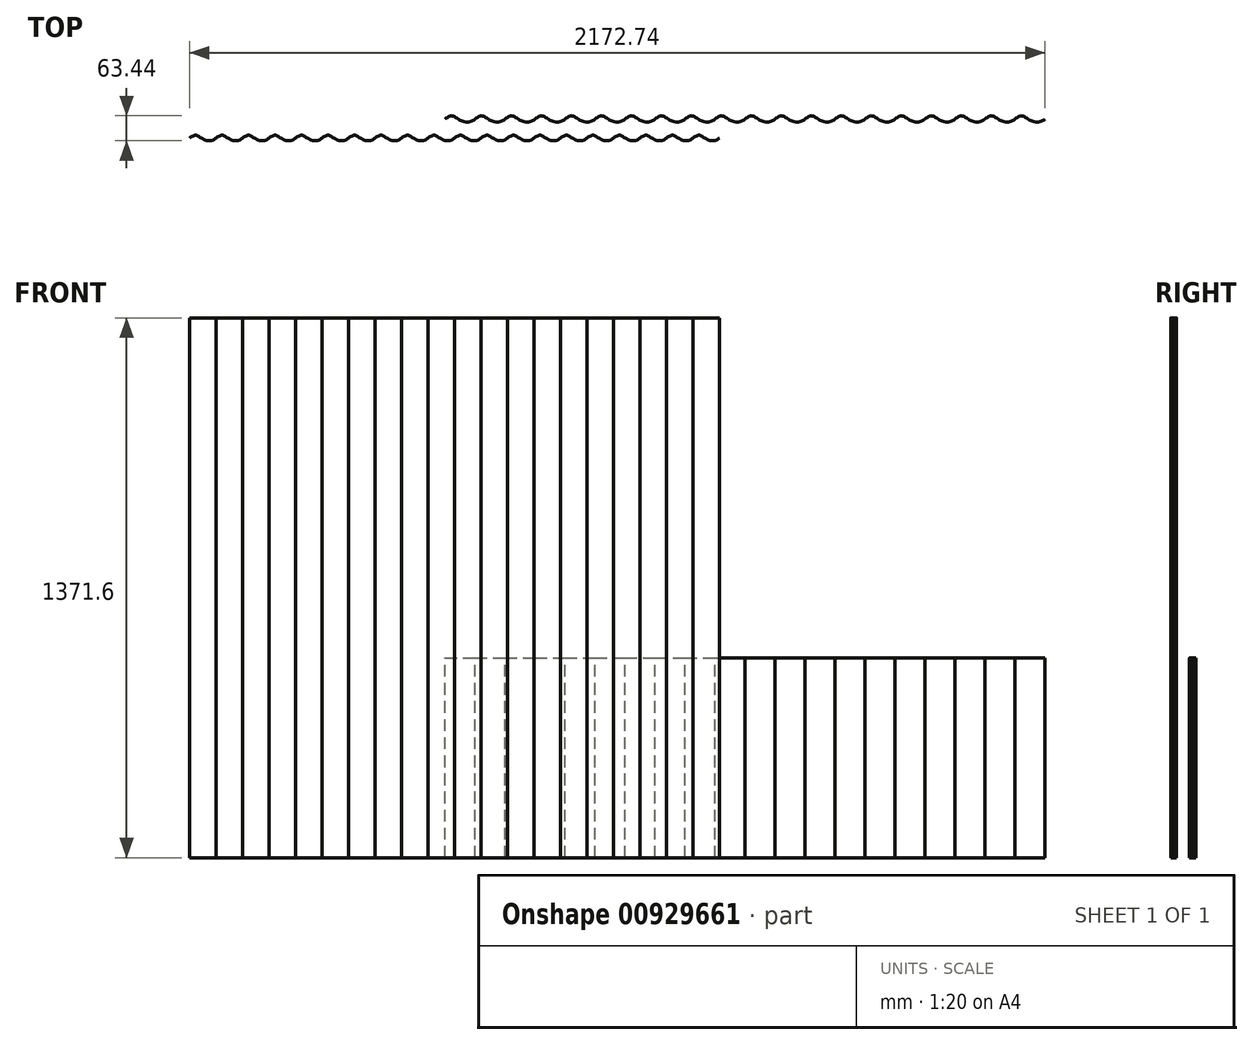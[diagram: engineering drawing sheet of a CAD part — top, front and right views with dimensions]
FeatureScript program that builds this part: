
annotation { "Feature Type Name" : "Feature", "Feature Type Description" : "" }
export const myFeature = defineFeature(function(context is Context, id is Id, definition is map)
    precondition{}
    {
        {
            var Q0;
            Q0=qCreatedBy(makeId("Top.planeOp"),FACE);
            var sketch = newSketch(context, id + "F0", { "sketchPlane" : qUnion([Q0])});
            skFitSpline(sketch, "E0", {"points": [v(-76.2, 0) * mm, v(-59.35, 8.43) * mm, v(-42.5, 0) * mm, v(-18.32, -7.7) * mm, v(0, 0) * mm], "startDerivative": vector(71.9, 53.55) * mm, "endDerivative": vector(70.3, 44.56) * mm});
            skFitSpline(sketch, "E1", {"points": [v(0, 0) * mm, v(16.85, 8.43) * mm, v(33.7, 0) * mm, v(57.88, -7.7) * mm, v(76.2, 0) * mm], "startDerivative": vector(71.9, 53.55) * mm, "endDerivative": vector(70.3, 44.56) * mm});
            skFitSpline(sketch, "E2", {"points": [v(76.2, 0) * mm, v(93.05, 8.43) * mm, v(109.9, 0) * mm, v(134.08, -7.7) * mm, v(152.4, 0) * mm], "startDerivative": vector(71.9, 53.55) * mm, "endDerivative": vector(70.3, 44.56) * mm});
            skFitSpline(sketch, "E3", {"points": [v(152.4, 0) * mm, v(169.25, 8.43) * mm, v(186.1, 0) * mm, v(210.28, -7.7) * mm, v(228.6, 0) * mm], "startDerivative": vector(71.9, 53.55) * mm, "endDerivative": vector(70.3, 44.56) * mm});
            skFitSpline(sketch, "E4", {"points": [v(228.6, 0) * mm, v(245.45, 8.43) * mm, v(262.3, 0) * mm, v(286.48, -7.7) * mm, v(304.8, 0) * mm], "startDerivative": vector(71.9, 53.55) * mm, "endDerivative": vector(70.3, 44.56) * mm});
            skFitSpline(sketch, "E5", {"points": [v(304.8, 0) * mm, v(321.65, 8.43) * mm, v(338.5, 0) * mm, v(362.68, -7.7) * mm, v(381, 0) * mm], "startDerivative": vector(71.9, 53.55) * mm, "endDerivative": vector(70.3, 44.56) * mm});
            skFitSpline(sketch, "E6", {"points": [v(381, 0) * mm, v(397.85, 8.43) * mm, v(414.7, 0) * mm, v(438.88, -7.7) * mm, v(457.2, 0) * mm], "startDerivative": vector(71.9, 53.55) * mm, "endDerivative": vector(70.3, 44.56) * mm});
            skFitSpline(sketch, "E7", {"points": [v(457.2, 0) * mm, v(474.05, 8.43) * mm, v(490.9, 0) * mm, v(515.08, -7.7) * mm, v(533.4, 0) * mm], "startDerivative": vector(71.9, 53.55) * mm, "endDerivative": vector(70.3, 44.56) * mm});
            skFitSpline(sketch, "E8", {"points": [v(533.4, 0) * mm, v(550.25, 8.43) * mm, v(567.1, 0) * mm, v(591.28, -7.7) * mm, v(609.6, 0) * mm], "startDerivative": vector(71.9, 53.55) * mm, "endDerivative": vector(70.3, 44.56) * mm});
            skFitSpline(sketch, "E9", {"points": [v(609.6, 0) * mm, v(626.45, 8.43) * mm, v(643.3, 0) * mm, v(667.48, -7.7) * mm, v(685.8, 0) * mm], "startDerivative": vector(71.9, 53.55) * mm, "endDerivative": vector(70.3, 44.56) * mm});
            skFitSpline(sketch, "E10", {"points": [v(685.8, 0) * mm, v(702.65, 8.43) * mm, v(719.5, 0) * mm, v(743.68, -7.7) * mm, v(762, 0) * mm], "startDerivative": vector(71.9, 53.55) * mm, "endDerivative": vector(70.3, 44.56) * mm});
            skFitSpline(sketch, "E11", {"points": [v(762, 0) * mm, v(778.85, 8.43) * mm, v(795.7, 0) * mm, v(819.88, -7.7) * mm, v(838.2, 0) * mm], "startDerivative": vector(71.9, 53.55) * mm, "endDerivative": vector(70.3, 44.56) * mm});
            skFitSpline(sketch, "E12", {"points": [v(838.2, 0) * mm, v(855.05, 8.43) * mm, v(871.9, 0) * mm, v(896.08, -7.7) * mm, v(914.4, 0) * mm], "startDerivative": vector(71.9, 53.55) * mm, "endDerivative": vector(70.3, 44.56) * mm});
            skFitSpline(sketch, "E13", {"points": [v(914.4, 0) * mm, v(931.25, 8.43) * mm, v(948.1, 0) * mm, v(972.28, -7.7) * mm, v(990.6, 0) * mm], "startDerivative": vector(71.9, 53.55) * mm, "endDerivative": vector(70.3, 44.56) * mm});
            skFitSpline(sketch, "E14", {"points": [v(990.6, 0) * mm, v(1007.45, 8.43) * mm, v(1024.3, 0) * mm, v(1048.48, -7.7) * mm, v(1066.8, 0) * mm], "startDerivative": vector(71.9, 53.55) * mm, "endDerivative": vector(70.3, 44.56) * mm});
            skFitSpline(sketch, "E15", {"points": [v(1066.8, 0) * mm, v(1083.65, 8.43) * mm, v(1100.5, 0) * mm, v(1124.68, -7.7) * mm, v(1143, 0) * mm], "startDerivative": vector(71.9, 53.55) * mm, "endDerivative": vector(70.3, 44.56) * mm});
            skFitSpline(sketch, "E16", {"points": [v(1143, 0) * mm, v(1159.85, 8.43) * mm, v(1176.7, 0) * mm, v(1200.88, -7.7) * mm, v(1219.2, 0) * mm], "startDerivative": vector(71.9, 53.55) * mm, "endDerivative": vector(70.3, 44.56) * mm});
            skFitSpline(sketch, "E17", {"points": [v(1219.2, 0) * mm, v(1236.05, 8.43) * mm, v(1252.9, 0) * mm, v(1277.08, -7.7) * mm, v(1295.4, 0) * mm], "startDerivative": vector(71.9, 53.55) * mm, "endDerivative": vector(70.3, 44.56) * mm});
            skFitSpline(sketch, "E18", {"points": [v(1295.4, 0) * mm, v(1312.25, 8.43) * mm, v(1329.1, 0) * mm, v(1353.28, -7.7) * mm, v(1371.6, 0) * mm], "startDerivative": vector(71.9, 53.55) * mm, "endDerivative": vector(70.3, 44.56) * mm});
            skFitSpline(sketch, "E19", {"points": [v(1371.6, 0) * mm, v(1388.45, 8.43) * mm, v(1405.3, 0) * mm, v(1429.48, -7.7) * mm, v(1447.8, 0) * mm], "startDerivative": vector(71.9, 53.55) * mm, "endDerivative": vector(70.3, 44.56) * mm});
            skSolve(sketch);
        }
        {
            var Q0;
            Q0=qCreatedBy(makeId("Top.planeOp"),FACE);
            var sketch = newSketch(context, id + "F1", { "sketchPlane" : qUnion([Q0])});
            skFitSpline(sketch, "E20", {"points": [v(-724.94, -48.18) * mm, v(-710.06, -40.73) * mm, v(-695.17, -48.18) * mm, v(-673.81, -54.97) * mm, v(-657.63, -48.18) * mm], "startDerivative": vector(63.5, 47.3) * mm, "endDerivative": vector(62.1, 39.37) * mm});
            skFitSpline(sketch, "E21", {"points": [v(-657.63, -48.18) * mm, v(-642.75, -40.73) * mm, v(-627.86, -48.18) * mm, v(-606.5, -54.97) * mm, v(-590.32, -48.18) * mm], "startDerivative": vector(63.5, 47.3) * mm, "endDerivative": vector(62.1, 39.37) * mm});
            skFitSpline(sketch, "E22", {"points": [v(-590.32, -48.18) * mm, v(-575.44, -40.73) * mm, v(-560.55, -48.18) * mm, v(-539.2, -54.97) * mm, v(-523.01, -48.18) * mm], "startDerivative": vector(63.5, 47.3) * mm, "endDerivative": vector(62.1, 39.37) * mm});
            skFitSpline(sketch, "E23", {"points": [v(-523.01, -48.18) * mm, v(-508.13, -40.73) * mm, v(-493.24, -48.18) * mm, v(-471.88, -54.97) * mm, v(-455.7, -48.18) * mm], "startDerivative": vector(63.5, 47.3) * mm, "endDerivative": vector(62.1, 39.37) * mm});
            skFitSpline(sketch, "E24", {"points": [v(-455.7, -48.18) * mm, v(-440.82, -40.73) * mm, v(-425.93, -48.18) * mm, v(-404.57, -54.97) * mm, v(-388.4, -48.18) * mm], "startDerivative": vector(63.5, 47.3) * mm, "endDerivative": vector(62.1, 39.37) * mm});
            skFitSpline(sketch, "E25", {"points": [v(-388.4, -48.18) * mm, v(-373.5, -40.73) * mm, v(-358.62, -48.18) * mm, v(-337.26, -54.97) * mm, v(-321.08, -48.18) * mm], "startDerivative": vector(63.5, 47.3) * mm, "endDerivative": vector(62.1, 39.37) * mm});
            skFitSpline(sketch, "E26", {"points": [v(-321.08, -48.18) * mm, v(-306.2, -40.73) * mm, v(-291.3, -48.18) * mm, v(-269.95, -54.97) * mm, v(-253.77, -48.18) * mm], "startDerivative": vector(63.5, 47.3) * mm, "endDerivative": vector(62.1, 39.37) * mm});
            skFitSpline(sketch, "E27", {"points": [v(-253.77, -48.18) * mm, v(-238.89, -40.73) * mm, v(-224, -48.18) * mm, v(-202.64, -54.97) * mm, v(-186.46, -48.18) * mm], "startDerivative": vector(63.5, 47.3) * mm, "endDerivative": vector(62.1, 39.37) * mm});
            skFitSpline(sketch, "E28", {"points": [v(-186.46, -48.18) * mm, v(-171.58, -40.73) * mm, v(-156.69, -48.18) * mm, v(-135.33, -54.97) * mm, v(-119.15, -48.18) * mm], "startDerivative": vector(63.5, 47.3) * mm, "endDerivative": vector(62.1, 39.37) * mm});
            skFitSpline(sketch, "E29", {"points": [v(-119.15, -48.18) * mm, v(-104.27, -40.73) * mm, v(-89.38, -48.18) * mm, v(-68.02, -54.97) * mm, v(-51.84, -48.18) * mm], "startDerivative": vector(63.5, 47.3) * mm, "endDerivative": vector(62.1, 39.37) * mm});
            skFitSpline(sketch, "E30", {"points": [v(-51.84, -48.18) * mm, v(-36.96, -40.73) * mm, v(-22.07, -48.18) * mm, v(-0.71, -54.97) * mm, v(15.47, -48.18) * mm], "startDerivative": vector(63.5, 47.3) * mm, "endDerivative": vector(62.1, 39.37) * mm});
            skFitSpline(sketch, "E31", {"points": [v(15.47, -48.18) * mm, v(30.35, -40.73) * mm, v(45.24, -48.18) * mm, v(66.6, -54.97) * mm, v(82.78, -48.18) * mm], "startDerivative": vector(63.5, 47.3) * mm, "endDerivative": vector(62.1, 39.37) * mm});
            skFitSpline(sketch, "E32", {"points": [v(82.78, -48.18) * mm, v(97.66, -40.73) * mm, v(112.55, -48.18) * mm, v(133.9, -54.97) * mm, v(150.09, -48.18) * mm], "startDerivative": vector(63.5, 47.3) * mm, "endDerivative": vector(62.1, 39.37) * mm});
            skFitSpline(sketch, "E33", {"points": [v(150.09, -48.18) * mm, v(164.97, -40.73) * mm, v(179.86, -48.18) * mm, v(201.22, -54.97) * mm, v(217.4, -48.18) * mm], "startDerivative": vector(63.5, 47.3) * mm, "endDerivative": vector(62.1, 39.37) * mm});
            skFitSpline(sketch, "E34", {"points": [v(217.4, -48.18) * mm, v(232.28, -40.73) * mm, v(247.17, -48.18) * mm, v(268.53, -54.97) * mm, v(284.7, -48.18) * mm], "startDerivative": vector(63.5, 47.3) * mm, "endDerivative": vector(62.1, 39.37) * mm});
            skFitSpline(sketch, "E35", {"points": [v(284.7, -48.18) * mm, v(299.6, -40.73) * mm, v(314.48, -48.18) * mm, v(335.84, -54.97) * mm, v(352.02, -48.18) * mm], "startDerivative": vector(63.5, 47.3) * mm, "endDerivative": vector(62.1, 39.37) * mm});
            skFitSpline(sketch, "E36", {"points": [v(352.02, -48.18) * mm, v(366.9, -40.73) * mm, v(381.8, -48.18) * mm, v(403.15, -54.97) * mm, v(419.33, -48.18) * mm], "startDerivative": vector(63.5, 47.3) * mm, "endDerivative": vector(62.1, 39.37) * mm});
            skFitSpline(sketch, "E37", {"points": [v(419.33, -48.18) * mm, v(434.21, -40.73) * mm, v(449.1, -48.18) * mm, v(470.46, -54.97) * mm, v(486.64, -48.18) * mm], "startDerivative": vector(63.5, 47.3) * mm, "endDerivative": vector(62.1, 39.37) * mm});
            skFitSpline(sketch, "E38", {"points": [v(486.64, -48.18) * mm, v(501.52, -40.73) * mm, v(516.41, -48.18) * mm, v(537.77, -54.97) * mm, v(553.95, -48.18) * mm], "startDerivative": vector(63.5, 47.3) * mm, "endDerivative": vector(62.1, 39.37) * mm});
            skFitSpline(sketch, "E39", {"points": [v(553.95, -48.18) * mm, v(568.83, -40.73) * mm, v(583.72, -48.18) * mm, v(605.08, -54.97) * mm, v(621.26, -48.18) * mm], "startDerivative": vector(63.5, 47.3) * mm, "endDerivative": vector(62.1, 39.37) * mm});
            skSolve(sketch);
        }
        {
            var Q0;
            Q0 = qSketchRegion(id + "F0", true);
            var Q1;
            Q1 = qConstructionFilter(qBodyType(qCreatedBy(id + "F0" ,EDGE), BodyType.WIRE), ConstructionObject.NO);
            extrude(context, id + "F2", {"entities" : qUnion([Q0]), "bodyType" : ToolBodyType.SURFACE, "operationType" : NewBodyOperationType.ADD, "surfaceEntities" : qUnion([Q1]), "depth" : 508 * mm, "offsetDistance" : 25.4 * mm});
        }
        {
            var Q0;
            Q0 = qSketchRegion(id + "F1", true);
            var Q1;
            Q1 = qConstructionFilter(qBodyType(qCreatedBy(id + "F1" ,EDGE), BodyType.WIRE), ConstructionObject.NO);
            extrude(context, id + "F3", {"entities" : qUnion([Q0]), "bodyType" : ToolBodyType.SURFACE, "surfaceEntities" : qUnion([Q1]), "depth" : 1371.6 * mm, "offsetDistance" : 25.4 * mm});
        }
    });
